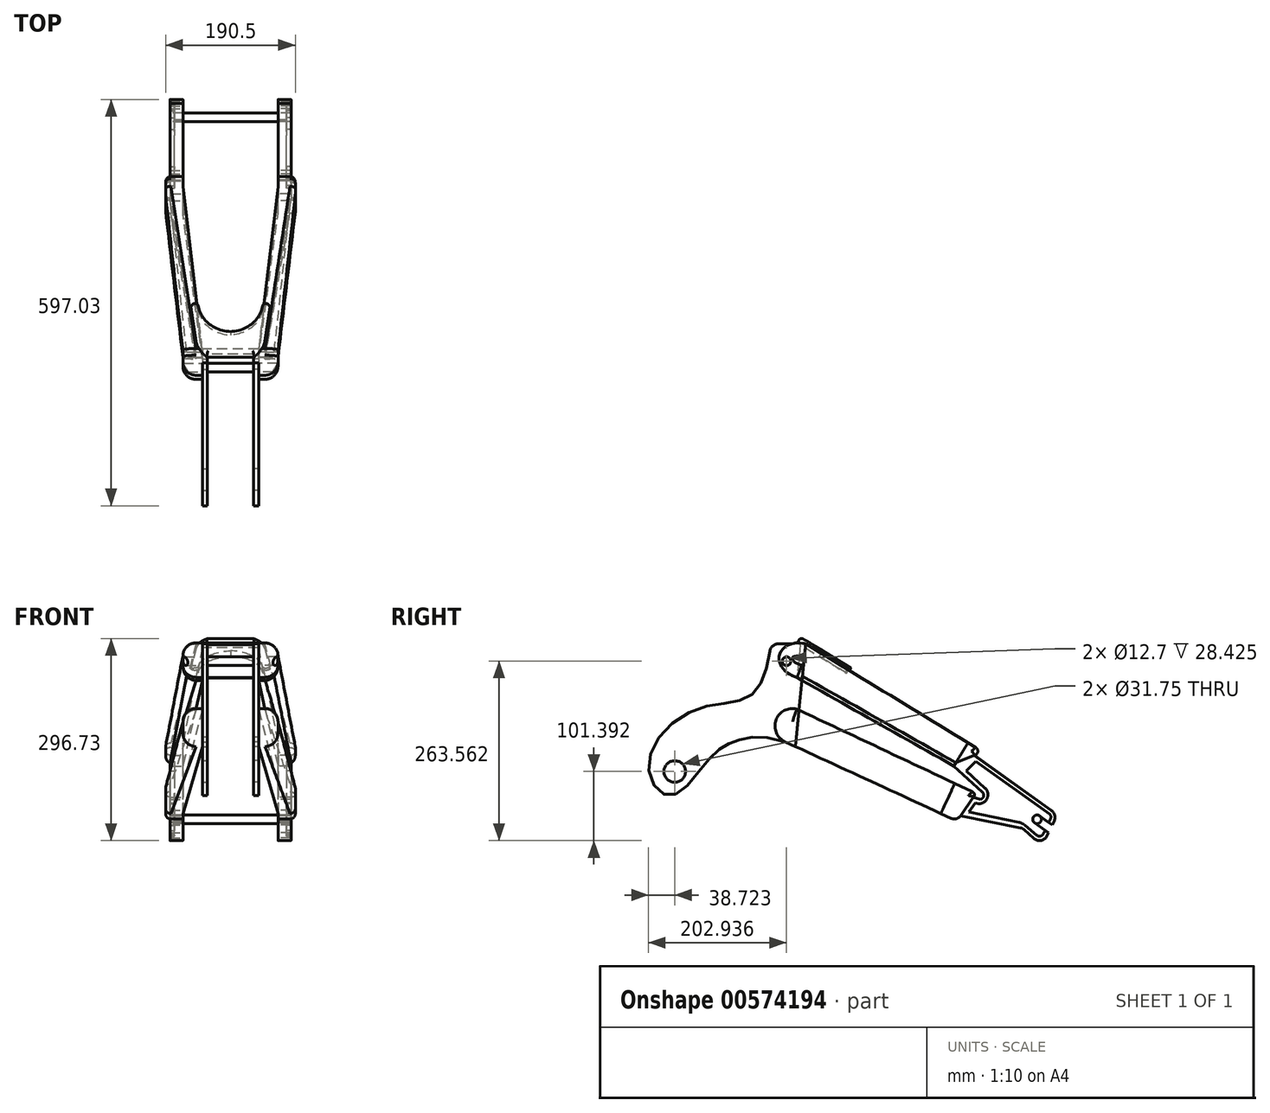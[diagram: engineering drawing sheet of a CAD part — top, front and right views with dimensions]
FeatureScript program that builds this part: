
annotation { "Feature Type Name" : "Feature", "Feature Type Description" : "" }
export const myFeature = defineFeature(function(context is Context, id is Id, definition is map)
    precondition{}
    {
        {
            var Q0;
            Q0=qCreatedBy(makeId("Right.planeOp"),FACE);
            var sketch = newSketch(context, id + "F0", { "sketchPlane" : qUnion([Q0])});
            skCircle(sketch, "E0", {"center": v(0, 0) * mm, "radius": 1.16 * mm, "construction": true});
            skLineSegment(sketch, "E1", {"start": v(-232.88, 679.32) * mm, "end": v(-270.07, 627.86) * mm, "construction": true});
            skLineSegment(sketch, "E2", {"start": v(-270.07, 627.86) * mm, "end": v(-307.27, 576.4) * mm, "construction": true});
            skLineSegment(sketch, "E3", {"start": v(-307.27, 576.4) * mm, "end": v(-723.9, 0) * mm, "construction": true});
            skLineSegment(sketch, "E4", {"start": v(-270.07, 627.86) * mm, "end": v(185.67, 350.7) * mm, "construction": true});
            skCircle(sketch, "E5", {"center": v(0, 0) * mm, "radius": 12.7 * mm});
            skCircle(sketch, "E6", {"center": v(-78.13, 64.95) * mm, "radius": 15.88 * mm});
            skLineSegment(sketch, "E7", {"start": v(-78.13, 64.95) * mm, "end": v(-64.36, 72.86) * mm, "construction": true});
            skLineSegment(sketch, "E8", {"start": v(107.04, 228.4) * mm, "end": v(360.88, 72.62) * mm, "construction": true});
            skLineSegment(sketch, "E9", {"start": v(360.88, 72.62) * mm, "end": v(465.2, 0) * mm, "construction": true});
            skPoint(sketch, "E10.middle", {"position": v(86.09, 227.12) * mm});
            skLineSegment(sketch, "E11", {"start": v(361.77, 88.47) * mm, "end": v(322.87, 73.33) * mm});
            skLineSegment(sketch, "E12", {"start": v(361.77, 88.47) * mm, "end": v(474.18, 8.33) * mm});
            skLineSegment(sketch, "E13.trimOffspring", {"start": v(435.13, -20.68) * mm, "end": v(448.92, -33.16) * mm});
            skPoint(sketch, "E14.visualSharp", {"position": v(485.86, 0) * mm});
            skPoint(sketch, "E15.visualSharp", {"position": v(461.59, -44.63) * mm});
            skArc(sketch, "E15.filletArc", {"start": v(448.92, -33.16) * mm, "mid": v(458.05, -36.43) * mm, "end": v(466.83, -32.3) * mm});
            skPoint(sketch, "E16.visualSharp", {"position": v(430.6, -16.57) * mm});
            skArc(sketch, "E16.filletArc", {"start": v(435.13, -20.68) * mm, "mid": v(432.34, -18.76) * mm, "end": v(429.13, -17.64) * mm});
            skPoint(sketch, "E17.visualSharp", {"position": v(384.46, 25.2) * mm});
            skCircle(sketch, "E18", {"center": v(0, 0) * mm, "radius": 22.23 * mm});
            skEllipticalArc(sketch, "E19", {});
            skLineSegment(sketch, "E20", {"start": v(132.64, 242.15) * mm, "end": v(363.9, 100.23) * mm});
            skLineSegment(sketch, "E21", {"start": v(101.4, 203.35) * mm, "end": v(311.62, 74.34) * mm});
            skLineSegment(sketch, "E22", {"start": v(362.88, 88.9) * mm, "end": v(322.87, 73.33) * mm});
            skPoint(sketch, "E23.visualSharp", {"position": v(317, 71.04) * mm});
            skArc(sketch, "E23.filletArc", {"start": v(311.62, 74.34) * mm, "mid": v(317.13, 72.52) * mm, "end": v(322.87, 73.33) * mm});
            skPoint(sketch, "E24.visualSharp", {"position": v(374.8, 93.54) * mm});
            skArc(sketch, "E24.filletArc", {"start": v(362.88, 88.9) * mm, "mid": v(366.9, 94.25) * mm, "end": v(363.9, 100.23) * mm});
            skLineSegment(sketch, "E25", {"start": v(326.7, 65.1) * mm, "end": v(352.54, 107.2) * mm});
            skArc(sketch, "E26.1", {"start": v(473.17, -5.57) * mm, "mid": v(474.21, -1.37) * mm, "end": v(472.33, 2.52) * mm});
            skLineSegment(sketch, "E26.2", {"start": v(364.06, 79.7) * mm, "end": v(472.33, 2.52) * mm});
            skLineSegment(sketch, "E26.3", {"start": v(364.06, 79.7) * mm, "end": v(349.79, 65.87) * mm});
            skArc(sketch, "E26.4", {"start": v(436.25, -14.18) * mm, "mid": v(432.06, -11.3) * mm, "end": v(427.25, -9.63) * mm});
            skLineSegment(sketch, "E26.8", {"start": v(353.82, 5.27) * mm, "end": v(427.25, -9.63) * mm});
            skLineSegment(sketch, "E26.9", {"start": v(353.82, 5.27) * mm, "end": v(353.82, 5.27) * mm});
            skLineSegment(sketch, "E26.10", {"start": v(353.82, 5.27) * mm, "end": v(363.3, 18.82) * mm});
            skLineSegment(sketch, "E26.13", {"start": v(349.79, 65.87) * mm, "end": v(377.5, 40.5) * mm});
            skArc(sketch, "E27", {"start": v(106.8, 154) * mm, "mid": v(105.6, 154.53) * mm, "end": v(104.38, 155) * mm});
            skPoint(sketch, "E28.visualSharp", {"position": v(367.54, 96.52) * mm});
            skPoint(sketch, "E29.visualSharp", {"position": v(357.72, 48.2) * mm});
            skPoint(sketch, "E30.0.internal.orphan", {"position": v(62.7, 11.08) * mm});
            skPoint(sketch, "E30.endDerivative.orphan", {"position": v(0, 109.86) * mm});
            skCircle(sketch, "E31", {"center": v(86.09, 227.12) * mm, "radius": 6.35 * mm});
            skArc(sketch, "E32", {"start": v(223.85, 186.17) * mm, "mid": v(173.06, 140.92) * mm, "end": v(132.63, 86.22) * mm, "construction": true});
            skLineSegment(sketch, "E33", {"start": v(93.24, 252.52) * mm, "end": v(74.1, 252.52) * mm});
            skFitSpline(sketch, "E34", {"points": [v(63.36, 252.52) * mm, v(34.16, 177.27) * mm, v(-50.36, 154.97) * mm, v(-116.85, 72.97) * mm, v(-84.09, 29.6) * mm, v(-25.78, 85.5) * mm, v(12.3, 109.86) * mm, v(83.95, 108.65) * mm], "startDerivative": vector(-99.71, -604.57) * mm, "endDerivative": vector(670.82, -241.51) * mm});
            skArc(sketch, "E35.filletArc", {"start": v(74.1, 252.52) * mm, "mid": v(65.93, 249.54) * mm, "end": v(61.59, 242) * mm});
            skPoint(sketch, "E36.orphan", {"position": v(114.16, 252.52) * mm});
            skPoint(sketch, "E37.trimOffspring.end.orphan", {"position": v(-64.8, 72.62) * mm});
            skPoint(sketch, "E38.endSnap0", {"position": v(466.83, -32.3) * mm});
            skArc(sketch, "E39.trimOffspring", {"start": v(478.77, -8.28) * mm, "mid": v(479.72, 0.92) * mm, "end": v(474.18, 8.33) * mm});
            skLineSegment(sketch, "E40", {"start": v(361.01, 27.86) * mm, "end": v(341.53, 0) * mm});
            skLineSegment(sketch, "E41", {"start": v(359.02, 35.33) * mm, "end": v(106.8, 154) * mm});
            skLineSegment(sketch, "E42", {"start": v(327.78, -3.72) * mm, "end": v(83.95, 108.65) * mm});
            skPoint(sketch, "E43.orphan", {"position": v(116.25, 146.34) * mm});
            skLineSegment(sketch, "E44", {"start": v(114.16, 252.52) * mm, "end": v(99.03, 101.7) * mm});
            skLineSegment(sketch, "E45", {"start": v(470.6, -9.4) * mm, "end": v(457.51, -0.07) * mm});
            skArc(sketch, "E46", {"start": v(457.51, -0.07) * mm, "mid": v(448.65, -1.55) * mm, "end": v(450.14, -10.4) * mm});
            skLineSegment(sketch, "E47", {"start": v(450.14, -10.4) * mm, "end": v(465.87, -21.62) * mm});
            skLineSegment(sketch, "E48", {"start": v(473.17, -5.57) * mm, "end": v(470.6, -9.4) * mm});
            skArc(sketch, "E49.0", {"start": v(453.18, -28.45) * mm, "mid": v(458.69, -29.97) * mm, "end": v(463.19, -26.45) * mm});
            skLineSegment(sketch, "E50", {"start": v(453.18, -28.45) * mm, "end": v(436.25, -14.18) * mm});
            skLineSegment(sketch, "E51", {"start": v(463.19, -26.45) * mm, "end": v(465.87, -21.62) * mm});
            skPoint(sketch, "E52.visualSharp", {"position": v(364.45, 32.77) * mm});
            skArc(sketch, "E52.filletArc", {"start": v(361.01, 27.86) * mm, "mid": v(361.75, 32.06) * mm, "end": v(359.02, 35.33) * mm});
            skPoint(sketch, "E53.visualSharp", {"position": v(336.21, -7.6) * mm});
            skArc(sketch, "E53.filletArc", {"start": v(327.78, -3.72) * mm, "mid": v(335.33, -4.36) * mm, "end": v(341.53, 0) * mm});
            skLineSegment(sketch, "E54", {"start": v(429.13, -17.64) * mm, "end": v(341.61, 0.12) * mm});
            skLineSegment(sketch, "E55", {"start": v(333.06, 47.54) * mm, "end": v(312.65, 3.25) * mm});
            skLineSegment(sketch, "E56", {"start": v(373.48, 34.8) * mm, "end": v(327.72, 76.68) * mm});
            skLineSegment(sketch, "E57", {"start": v(478.77, -8.28) * mm, "end": v(476.22, -13.4) * mm});
            skLineSegment(sketch, "E58", {"start": v(465.87, -21.62) * mm, "end": v(470.5, -24.92) * mm});
            skLineSegment(sketch, "E59", {"start": v(470.6, -9.4) * mm, "end": v(476.22, -13.4) * mm});
            skLineSegment(sketch, "E60.trimOffspring", {"start": v(470.5, -24.92) * mm, "end": v(466.83, -32.3) * mm});
            skLineSegment(sketch, "E61", {"start": v(106.8, 154) * mm, "end": v(101.05, 156.7) * mm});
            skArc(sketch, "E62", {"start": v(101.05, 156.7) * mm, "mid": v(70.54, 140.5) * mm, "end": v(83.95, 108.65) * mm});
            skLineSegment(sketch, "E63", {"start": v(370.63, 24.07) * mm, "end": v(360.23, 26.98) * mm});
            skLineSegment(sketch, "E64", {"start": v(101.4, 203.35) * mm, "end": v(106.46, 253.8) * mm});
            skLineSegment(sketch, "E65", {"start": v(132.64, 242.15) * mm, "end": v(114.16, 252.52) * mm});
            skArc(sketch, "E66", {"start": v(370.63, 24.07) * mm, "mid": v(375.3, 28.58) * mm, "end": v(373.48, 34.8) * mm});
            skLineSegment(sketch, "E67", {"start": v(363.3, 18.82) * mm, "end": v(367.7, 17.76) * mm});
            skArc(sketch, "E68", {"start": v(367.7, 17.76) * mm, "mid": v(380.7, 25.64) * mm, "end": v(377.5, 40.5) * mm});
            const initialGuessF0  = {"E19": [0.10777975644892944, 0.22793694152375826, 0.25127126595347304, 0.967916706595221, 0.0254, 0.03324043917130964, 6.283185307179586, 3.141592653589793]};
            skSetInitialGuess(sketch, initialGuessF0);
            skSolve(sketch);
        }
        {
            var Q0;
            Q0=makeQuery(id+"F0.imprint","IMPRINT",FACE,{"disambiguationData":[TD([[makeQuery(id+"F0.imprint","IMPRINT",EDGE,{"derivedFrom":sQuery(id+"F0.wireOp",EDGE,"E6")}),-1.0]])]});
            var Q1;
            {var subQ3=sQuery(id+"F0.wireOp",EDGE,"E64");Q1=makeQuery(id+"F0.imprint","IMPRINT",FACE,{"disambiguationData":[TD([[makeQuery(id+"F0.imprint","IMPRINT",EDGE,{"derivedFrom":subQ3}),-1.0]])]});}
            var Q2;
            {var subQ2=sQuery(id+"F0.wireOp",EDGE,"E64");Q2=makeQuery(id+"F0.imprint","IMPRINT",FACE,{"disambiguationData":[TD([[makeQuery(id+"F0.imprint","IMPRINT",EDGE,{"derivedFrom":subQ2}),1.0]])]});}
            var Q3;
            {var subQ0=sQuery(id+"F0.wireOp",EDGE,"E62");Q3=makeQuery(id+"F0.imprint","IMPRINT",FACE,{"disambiguationData":[TD([[makeQuery(id+"F0.imprint","IMPRINT",EDGE,{"derivedFrom":subQ0}),1.0]])]});}
            extrude(context, id + "F1", {"entities" : qUnion([Q0, Q1, Q2, Q3]), "oppositeDirection" : true, "depth" : 41.27 * mm, "offsetDistance" : 25.4 * mm, "hasSecondDirection" : true, "secondDirectionOppositeDirection" : true, "secondDirectionDepth" : 34 * mm});
        }
        {
            var Q0;
            {var subQ2=sQuery(id+"F0.wireOp",EDGE,"E64");Q0=makeQuery(id+"F0.imprint","IMPRINT",FACE,{"disambiguationData":[TD([[makeQuery(id+"F0.imprint","IMPRINT",EDGE,{"derivedFrom":subQ2}),1.0]])]});}
            var Q1;
            {var subQ3=sQuery(id+"F0.wireOp",EDGE,"E64");Q1=makeQuery(id+"F0.imprint","IMPRINT",FACE,{"disambiguationData":[TD([[makeQuery(id+"F0.imprint","IMPRINT",EDGE,{"derivedFrom":subQ3}),-1.0]])]});}
            var Q2;
            Q2=makeQuery(id+"F1.opExtrude","CAP_FACE",FACE,{"disambiguationData":[OSD([sQuery(id+"F0.wireOp",EDGE,"E6"),sQuery(id+"F0.wireOp",EDGE,"E19"),sQuery(id+"F0.wireOp",EDGE,"E31"),sQuery(id+"F0.wireOp",EDGE,"E33"),sQuery(id+"F0.wireOp",EDGE,"E34"),sQuery(id+"F0.wireOp",EDGE,"E35.filletArc"),sQuery(id+"F0.wireOp",EDGE,"E42"),sQuery(id+"F0.wireOp",EDGE,"E44")])],"isStart":false});
            var Q3;
            Q3=makeQuery(id+"F1.opExtrude","CAP_FACE",FACE,{"disambiguationData":[OSD([sQuery(id+"F0.wireOp",EDGE,"E6"),sQuery(id+"F0.wireOp",EDGE,"E19"),sQuery(id+"F0.wireOp",EDGE,"E31"),sQuery(id+"F0.wireOp",EDGE,"E33"),sQuery(id+"F0.wireOp",EDGE,"E34"),sQuery(id+"F0.wireOp",EDGE,"E35.filletArc"),sQuery(id+"F0.wireOp",EDGE,"E42"),sQuery(id+"F0.wireOp",EDGE,"E44")])],"isStart":false});
            extrude(context, id + "F2", {"entities" : qUnion([Q0, Q1]), "oppositeDirection" : true, "depth" : 69.85 * mm, "endBoundEntityFace" : qUnion([Q2]), "offsetDistance" : 25.4 * mm, "hasSecondDirection" : true, "secondDirectionOppositeDirection" : true, "secondDirectionDepth" : 41.27 * mm, "secondDirectionBoundEntityFace" : qUnion([Q3])});
        }
        {
            var Q0;
            {var subQ0=sQuery(id+"F0.wireOp",EDGE,"E62");Q0=makeQuery(id+"F0.imprint","IMPRINT",FACE,{"disambiguationData":[TD([[makeQuery(id+"F0.imprint","IMPRINT",EDGE,{"derivedFrom":subQ0}),1.0]])]});}
            var Q1;
            Q1=makeQuery(id+"F1.opExtrude","CAP_FACE",FACE,{"disambiguationData":[OSD([sQuery(id+"F0.wireOp",EDGE,"E6"),sQuery(id+"F0.wireOp",EDGE,"E19"),sQuery(id+"F0.wireOp",EDGE,"E31"),sQuery(id+"F0.wireOp",EDGE,"E33"),sQuery(id+"F0.wireOp",EDGE,"E34"),sQuery(id+"F0.wireOp",EDGE,"E35.filletArc"),sQuery(id+"F0.wireOp",EDGE,"E42"),sQuery(id+"F0.wireOp",EDGE,"E44")])],"isStart":false});
            extrude(context, id + "F3", {"entities" : qUnion([Q0]), "oppositeDirection" : true, "depth" : 69.85 * mm, "offsetDistance" : 25.4 * mm, "hasSecondDirection" : true, "secondDirectionBound" : BoundingType.UP_TO_SURFACE, "secondDirectionOppositeDirection" : true, "secondDirectionDepth" : 41.27 * mm, "secondDirectionBoundEntityFace" : qUnion([Q1])});
        }
        {
            var Q0;
            Q0=makeQuery(id+"F3.opExtrude","CAP_EDGE",EDGE,{"disambiguationData":[OSD([sQuery(id+"F0.wireOp",EDGE,"E42")])],"isStart":false});
            var Q1;
            Q1=makeQuery(id+"F3.opExtrude","CAP_EDGE",EDGE,{"disambiguationData":[OSD([sQuery(id+"F0.wireOp",EDGE,"E62")])],"isStart":false});
            var Q2;
            Q2=makeQuery(id+"F3.opExtrude","CAP_EDGE",EDGE,{"disambiguationData":[OSD([sQuery(id+"F0.wireOp",EDGE,"E61")])],"isStart":false});
            fillet(context, id + "F4", {"entities" : qUnion([Q0, Q1, Q2]), "radius" : 19.05 * mm, "tangentPropagation" : true, "allowEdgeOverflow" : false});
        }
        {
            var Q0;
            Q0=makeQuery(id+"F2.opExtrude","CAP_EDGE",EDGE,{"disambiguationData":[OSD([sQuery(id+"F0.wireOp",EDGE,"E19")])],"isStart":false});
            var Q1;
            Q1=makeQuery(id+"F2.opExtrude","CAP_EDGE",EDGE,{"disambiguationData":[OSD([sQuery(id+"F0.wireOp",EDGE,"E21")])],"isStart":false});
            var Q2;
            Q2=makeQuery(id+"F2.opExtrude","CAP_EDGE",EDGE,{"disambiguationData":[OSD([sQuery(id+"F0.wireOp",EDGE,"E62")])],"isStart":false});
            var Q3;
            Q3=makeQuery(id+"F2.opExtrude","CAP_EDGE",EDGE,{"disambiguationData":[OSD([sQuery(id+"F0.wireOp",EDGE,"E42")])],"isStart":false});
            var Q4;
            Q4=makeQuery(id+"F2.opExtrude","CAP_EDGE",EDGE,{"disambiguationData":[OSD([sQuery(id+"F0.wireOp",EDGE,"E61")])],"isStart":false});
            fillet(context, id + "F5", {"entities" : qUnion([Q0, Q1, Q2, Q3, Q4]), "radius" : 19.05 * mm, "tangentPropagation" : true, "allowEdgeOverflow" : false});
        }
        {
            var Q0;
            {var subQ2=sQuery(id+"F0.wireOp",EDGE,"E12");Q0=makeQuery(id+"F0.imprint","IMPRINT",FACE,{"disambiguationData":[TD([[makeQuery(id+"F0.imprint","IMPRINT",EDGE,{"derivedFrom":subQ2}),-1.0]])]});}
            extrude(context, id + "F6", {"entities" : qUnion([Q0]), "oppositeDirection" : true, "depth" : 82.55 * mm, "offsetDistance" : 25.4 * mm, "hasSecondDirection" : true, "secondDirectionOppositeDirection" : true, "secondDirectionDepth" : 69.85 * mm});
        }
        {
            var Q0;
            {var subQ8=sQuery(id+"F0.wireOp",EDGE,"E12");Q0=makeQuery(id+"F0.imprint","IMPRINT",FACE,{"disambiguationData":[TD([[makeQuery(id+"F0.imprint","IMPRINT",EDGE,{"derivedFrom":subQ8}),-1.0]])]});}
            var Q1;
            Q1=makeQuery(id+"F6.opExtrude","CAP_FACE",FACE,{"disambiguationData":[OSD([sQuery(id+"F0.wireOp",EDGE,"E12"),sQuery(id+"F0.wireOp",EDGE,"M1xsbYhA-3GXW-TK3J-AiRY-MQwu2QjJ6JFv"),sQuery(id+"F0.wireOp",EDGE,"fftMuAfU-lyxI-JiHh-AROv-P9D5QgGa0bzV"),sQuery(id+"F0.wireOp",EDGE,"pFgT3zMJ-KOq2-b6Dw-mOYE-cKnottaSpSPs"),sQuery(id+"F0.wireOp",EDGE,"Kr73LZLk-hWS2-4xuN-lAFo-ImR0NY1b2jm2"),sQuery(id+"F0.wireOp",EDGE,"o7p56DB6-jSA5-HMdE-oMg3-rrhRXBAi4A6l"),sQuery(id+"F0.wireOp",EDGE,"3QQUFEwI-nFqo-oOJl-WeC0-8RtVsm6bbfu0"),sQuery(id+"F0.wireOp",EDGE,"E13.trimOffspring"),sQuery(id+"F0.wireOp",EDGE,"E14.filletArc"),sQuery(id+"F0.wireOp",EDGE,"E15.filletArc"),sQuery(id+"F0.wireOp",EDGE,"E16.filletArc"),sQuery(id+"F0.wireOp",EDGE,"E17.filletArc"),sQuery(id+"F0.wireOp",EDGE,"97rRG8dY-9QWF-S3jQ-TL0d-bcv7SxNfUhuE"),sQuery(id+"F0.wireOp",EDGE,"4e05d5bf-7781-4494-8613-2b51d00994fc"),sQuery(id+"F0.wireOp",EDGE,"fBmHlY9h-KOnv-hHaG-drBH-S4dukekwon05"),sQuery(id+"F0.wireOp",EDGE,"960b2066-a2d9-46c6-8008-59963f1efdcf.trimOffspring"),sQuery(id+"F0.wireOp",EDGE,"E22")])],"isStart":true});
            extrude(context, id + "F7", {"entities" : qUnion([Q0]), "operationType" : NewBodyOperationType.ADD, "oppositeDirection" : true, "depth" : 88.9 * mm, "offsetDistance" : 25.4 * mm, "hasSecondDirection" : true, "secondDirectionOppositeDirection" : true, "secondDirectionDepth" : 69.85 * mm, "secondDirectionBoundEntityFace" : qUnion([Q1])});
        }
        {
            var Q0;
            Q0=makeQuery(id+"F0.imprint","IMPRINT",FACE,{"disambiguationData":[TD([[makeQuery(id+"F0.imprint","IMPRINT",EDGE,{"derivedFrom":sQuery(id+"F0.wireOp",EDGE,"E26.1")}),1.0]])]});
            var Q1;
            Q1=makeQuery(id+"F6.opExtrude","CAP_FACE",FACE,{"disambiguationData":[OSD([sQuery(id+"F0.wireOp",EDGE,"E12"),sQuery(id+"F0.wireOp",EDGE,"pFgT3zMJ-KOq2-b6Dw-mOYE-cKnottaSpSPs"),sQuery(id+"F0.wireOp",EDGE,"Kr73LZLk-hWS2-4xuN-lAFo-ImR0NY1b2jm2"),sQuery(id+"F0.wireOp",EDGE,"o7p56DB6-jSA5-HMdE-oMg3-rrhRXBAi4A6l"),sQuery(id+"F0.wireOp",EDGE,"3QQUFEwI-nFqo-oOJl-WeC0-8RtVsm6bbfu0"),sQuery(id+"F0.wireOp",EDGE,"E13.trimOffspring"),sQuery(id+"F0.wireOp",EDGE,"E14.filletArc"),sQuery(id+"F0.wireOp",EDGE,"E15.filletArc"),sQuery(id+"F0.wireOp",EDGE,"E16.filletArc"),sQuery(id+"F0.wireOp",EDGE,"E17.filletArc"),sQuery(id+"F0.wireOp",EDGE,"97rRG8dY-9QWF-S3jQ-TL0d-bcv7SxNfUhuE"),sQuery(id+"F0.wireOp",EDGE,"fBmHlY9h-KOnv-hHaG-drBH-S4dukekwon05"),sQuery(id+"F0.wireOp",EDGE,"960b2066-a2d9-46c6-8008-59963f1efdcf.trimOffspring"),sQuery(id+"F0.wireOp",EDGE,"E22"),sQuery(id+"F0.wireOp",EDGE,"E26.0"),sQuery(id+"F0.wireOp",EDGE,"E26.1"),sQuery(id+"F0.wireOp",EDGE,"E26.2"),sQuery(id+"F0.wireOp",EDGE,"E26.3"),sQuery(id+"F0.wireOp",EDGE,"E26.4"),sQuery(id+"F0.wireOp",EDGE,"E26.5"),sQuery(id+"F0.wireOp",EDGE,"E26.6"),sQuery(id+"F0.wireOp",EDGE,"E26.7"),sQuery(id+"F0.wireOp",EDGE,"E26.8"),sQuery(id+"F0.wireOp",EDGE,"E26.9"),sQuery(id+"F0.wireOp",EDGE,"E26.10"),sQuery(id+"F0.wireOp",EDGE,"E26.11"),sQuery(id+"F0.wireOp",EDGE,"E26.12"),sQuery(id+"F0.wireOp",EDGE,"E26.13"),sQuery(id+"F0.wireOp",EDGE,"oD7H4SGl-vte9-Riyu-Gu8U-rxnYaFvigUeV")])],"isStart":true});
            extrude(context, id + "F8", {"entities" : qUnion([Q0]), "operationType" : NewBodyOperationType.ADD, "oppositeDirection" : true, "depth" : 82.55 * mm, "offsetDistance" : 25.4 * mm, "hasSecondDirection" : true, "secondDirectionBound" : BoundingType.UP_TO_SURFACE, "secondDirectionOppositeDirection" : true, "secondDirectionDepth" : 25.4 * mm, "secondDirectionBoundEntityFace" : qUnion([Q1])});
        }
        {
            var Q0;
            {var subQ5=sQuery(id+"F0.wireOp",EDGE,"E24.filletArc");Q0=makeQuery(id+"F0.imprint","IMPRINT",FACE,{"disambiguationData":[TD([[makeQuery(id+"F0.imprint","IMPRINT",EDGE,{"derivedFrom":subQ5}),1.0]])]});}
            var Q1;
            {var subQ0=sQuery(id+"F0.wireOp",EDGE,"oD7H4SGl-vte9-Riyu-Gu8U-rxnYaFvigUeV");var subQ1=sQuery(id+"F0.wireOp",EDGE,"E26.13");var subQ2=sQuery(id+"F0.wireOp",EDGE,"E26.12");var subQ3=sQuery(id+"F0.wireOp",EDGE,"E26.11");var subQ4=sQuery(id+"F0.wireOp",EDGE,"E26.10");var subQ5=sQuery(id+"F0.wireOp",EDGE,"E26.9");var subQ6=sQuery(id+"F0.wireOp",EDGE,"E26.8");var subQ7=sQuery(id+"F0.wireOp",EDGE,"E26.7");var subQ8=sQuery(id+"F0.wireOp",EDGE,"E26.6");var subQ9=sQuery(id+"F0.wireOp",EDGE,"E26.5");var subQ10=sQuery(id+"F0.wireOp",EDGE,"E26.4");var subQ11=sQuery(id+"F0.wireOp",EDGE,"E26.3");var subQ12=sQuery(id+"F0.wireOp",EDGE,"E26.2");var subQ13=sQuery(id+"F0.wireOp",EDGE,"E26.1");var subQ14=sQuery(id+"F0.wireOp",EDGE,"E26.0");var subQ15=sQuery(id+"F0.wireOp",EDGE,"E22");var subQ16=sQuery(id+"F0.wireOp",EDGE,"960b2066-a2d9-46c6-8008-59963f1efdcf.trimOffspring");var subQ17=sQuery(id+"F0.wireOp",EDGE,"fBmHlY9h-KOnv-hHaG-drBH-S4dukekwon05");var subQ18=sQuery(id+"F0.wireOp",EDGE,"97rRG8dY-9QWF-S3jQ-TL0d-bcv7SxNfUhuE");var subQ19=sQuery(id+"F0.wireOp",EDGE,"E17.filletArc");var subQ20=sQuery(id+"F0.wireOp",EDGE,"E16.filletArc");var subQ21=sQuery(id+"F0.wireOp",EDGE,"E15.filletArc");var subQ22=sQuery(id+"F0.wireOp",EDGE,"E14.filletArc");var subQ23=sQuery(id+"F0.wireOp",EDGE,"E13.trimOffspring");var subQ24=sQuery(id+"F0.wireOp",EDGE,"3QQUFEwI-nFqo-oOJl-WeC0-8RtVsm6bbfu0");var subQ25=sQuery(id+"F0.wireOp",EDGE,"o7p56DB6-jSA5-HMdE-oMg3-rrhRXBAi4A6l");var subQ26=sQuery(id+"F0.wireOp",EDGE,"Kr73LZLk-hWS2-4xuN-lAFo-ImR0NY1b2jm2");var subQ27=sQuery(id+"F0.wireOp",EDGE,"pFgT3zMJ-KOq2-b6Dw-mOYE-cKnottaSpSPs");var subQ28=sQuery(id+"F0.wireOp",EDGE,"E12");Q1=makeQuery(id+"F8.boolean.opBoolean","MERGE",FACE,{"derivedFrom":[makeQuery(id+"F6.opExtrude","CAP_FACE",FACE,{"disambiguationData":[OSD([subQ28,subQ27,subQ26,subQ25,subQ24,subQ23,subQ22,subQ21,subQ20,subQ19,subQ18,subQ17,subQ16,subQ15,subQ14,subQ13,subQ12,subQ11,subQ10,subQ9,subQ8,subQ7,subQ6,subQ5,subQ4,subQ3,subQ2,subQ1,subQ0])],"isStart":true}),makeQuery(id+"F8.opExtrude","CAP_FACE",FACE,{"disambiguationData":[OSD([subQ28,subQ27,subQ26,subQ25,subQ24,subQ23,subQ22,subQ21,subQ20,subQ19,subQ18,subQ17,subQ16,subQ15,subQ14,subQ13,subQ12,subQ11,subQ10,subQ9,subQ8,subQ7,subQ6,subQ5,subQ4,subQ3,subQ2,subQ1,subQ0])],"isStart":true})]});}
            extrude(context, id + "F9", {"entities" : qUnion([Q0]), "operationType" : NewBodyOperationType.ADD, "oppositeDirection" : true, "depth" : 95.25 * mm, "offsetDistance" : 25.4 * mm, "hasSecondDirection" : true, "secondDirectionBound" : BoundingType.UP_TO_SURFACE, "secondDirectionOppositeDirection" : true, "secondDirectionDepth" : 25.4 * mm, "secondDirectionBoundEntityFace" : qUnion([Q1])});
        }
        {
            var Q0;
            Q0=makeQuery(id+"F9.opExtrude","CAP_EDGE",EDGE,{"disambiguationData":[OSD([sQuery(id+"F0.wireOp",EDGE,"E20")])],"isStart":false});
            fillet(context, id + "F10", {"entities" : qUnion([Q0]), "radius" : 7.62 * mm, "tangentPropagation" : true, "allowEdgeOverflow" : false});
        }
        {
            var Q0;
            {var subQ5=sQuery(id+"F0.wireOp",EDGE,"E40");Q0=makeQuery(id+"F0.imprint","IMPRINT",FACE,{"disambiguationData":[TD([[makeQuery(id+"F0.imprint","IMPRINT",EDGE,{"derivedFrom":subQ5}),-1.0]])]});}
            var Q1;
            {var subQ0=sQuery(id+"F0.wireOp",EDGE,"oD7H4SGl-vte9-Riyu-Gu8U-rxnYaFvigUeV");var subQ1=sQuery(id+"F0.wireOp",EDGE,"E26.13");var subQ2=sQuery(id+"F0.wireOp",EDGE,"E26.12");var subQ3=sQuery(id+"F0.wireOp",EDGE,"E26.11");var subQ4=sQuery(id+"F0.wireOp",EDGE,"E26.10");var subQ5=sQuery(id+"F0.wireOp",EDGE,"E26.9");var subQ6=sQuery(id+"F0.wireOp",EDGE,"E26.8");var subQ7=sQuery(id+"F0.wireOp",EDGE,"E26.7");var subQ8=sQuery(id+"F0.wireOp",EDGE,"E26.6");var subQ9=sQuery(id+"F0.wireOp",EDGE,"E26.5");var subQ10=sQuery(id+"F0.wireOp",EDGE,"E26.4");var subQ11=sQuery(id+"F0.wireOp",EDGE,"E26.3");var subQ12=sQuery(id+"F0.wireOp",EDGE,"E26.2");var subQ13=sQuery(id+"F0.wireOp",EDGE,"E26.1");var subQ14=sQuery(id+"F0.wireOp",EDGE,"E26.0");var subQ15=sQuery(id+"F0.wireOp",EDGE,"E22");var subQ16=sQuery(id+"F0.wireOp",EDGE,"960b2066-a2d9-46c6-8008-59963f1efdcf.trimOffspring");var subQ17=sQuery(id+"F0.wireOp",EDGE,"fBmHlY9h-KOnv-hHaG-drBH-S4dukekwon05");var subQ18=sQuery(id+"F0.wireOp",EDGE,"97rRG8dY-9QWF-S3jQ-TL0d-bcv7SxNfUhuE");var subQ19=sQuery(id+"F0.wireOp",EDGE,"E17.filletArc");var subQ20=sQuery(id+"F0.wireOp",EDGE,"E16.filletArc");var subQ21=sQuery(id+"F0.wireOp",EDGE,"E15.filletArc");var subQ22=sQuery(id+"F0.wireOp",EDGE,"E14.filletArc");var subQ23=sQuery(id+"F0.wireOp",EDGE,"E13.trimOffspring");var subQ24=sQuery(id+"F0.wireOp",EDGE,"3QQUFEwI-nFqo-oOJl-WeC0-8RtVsm6bbfu0");var subQ25=sQuery(id+"F0.wireOp",EDGE,"o7p56DB6-jSA5-HMdE-oMg3-rrhRXBAi4A6l");var subQ26=sQuery(id+"F0.wireOp",EDGE,"Kr73LZLk-hWS2-4xuN-lAFo-ImR0NY1b2jm2");var subQ27=sQuery(id+"F0.wireOp",EDGE,"pFgT3zMJ-KOq2-b6Dw-mOYE-cKnottaSpSPs");var subQ28=sQuery(id+"F0.wireOp",EDGE,"E12");Q1=makeQuery(id+"F9.boolean.opBoolean","MERGE",FACE,{"derivedFrom":[makeQuery(id+"F8.boolean.opBoolean","MERGE",FACE,{"derivedFrom":[makeQuery(id+"F6.opExtrude","CAP_FACE",FACE,{"disambiguationData":[OSD([subQ28,subQ27,subQ26,subQ25,subQ24,subQ23,subQ22,subQ21,subQ20,subQ19,subQ18,subQ17,subQ16,subQ15,subQ14,subQ13,subQ12,subQ11,subQ10,subQ9,subQ8,subQ7,subQ6,subQ5,subQ4,subQ3,subQ2,subQ1,subQ0])],"isStart":true}),makeQuery(id+"F8.opExtrude","CAP_FACE",FACE,{"disambiguationData":[OSD([subQ28,subQ27,subQ26,subQ25,subQ24,subQ23,subQ22,subQ21,subQ20,subQ19,subQ18,subQ17,subQ16,subQ15,subQ14,subQ13,subQ12,subQ11,subQ10,subQ9,subQ8,subQ7,subQ6,subQ5,subQ4,subQ3,subQ2,subQ1,subQ0])],"isStart":true})]}),makeQuery(id+"F9.opExtrude","CAP_FACE",FACE,{"disambiguationData":[OSD([subQ28,subQ27,subQ26,subQ25,subQ24,subQ23,subQ22,subQ21,subQ20,subQ19,subQ18,subQ17,subQ16,subQ15,subQ14,subQ13,subQ12,subQ11,subQ10,subQ9,subQ8,subQ7,subQ6,subQ5,subQ4,subQ3,subQ2,subQ1,subQ0])],"isStart":true})]});}
            extrude(context, id + "F11", {"entities" : qUnion([Q0]), "operationType" : NewBodyOperationType.ADD, "oppositeDirection" : true, "depth" : 95.25 * mm, "offsetDistance" : 25.4 * mm, "hasSecondDirection" : true, "secondDirectionBound" : BoundingType.UP_TO_SURFACE, "secondDirectionOppositeDirection" : true, "secondDirectionDepth" : 25.4 * mm, "secondDirectionBoundEntityFace" : qUnion([Q1])});
        }
        {
            var Q0;
            Q0=makeQuery(id+"F11.opExtrude","CAP_EDGE",EDGE,{"disambiguationData":[OSD([sQuery(id+"F0.wireOp",EDGE,"E40")])],"isStart":false});
            fillet(context, id + "F12", {"entities" : qUnion([Q0]), "radius" : 7.62 * mm, "tangentPropagation" : true, "allowEdgeOverflow" : false});
        }
        {
            var Q0;
            Q0=makeQuery(id+"F2.opExtrude","SWEPT_FACE",FACE,{"disambiguationData":[OSD([sQuery(id+"F0.wireOp",EDGE,"E44")])]});
            var Q1;
            Q1=makeQuery(id+"F9.opExtrude","SWEPT_FACE",FACE,{"disambiguationData":[OSD([sQuery(id+"F0.wireOp",EDGE,"E25")])]});
            loft(context, id + "F13", {"sheetProfilesArray" : [{ "sheetProfileEntities" : qUnion([Q0]) }, { "sheetProfileEntities" : qUnion([Q1]) }]});
        }
        {
            var Q0;
            Q0=makeQuery(id+"F3.opExtrude","SWEPT_FACE",FACE,{"disambiguationData":[OSD([sQuery(id+"F0.wireOp",EDGE,"E44")])]});
            var Q1;
            Q1=makeQuery(id+"F11.opExtrude","SWEPT_FACE",FACE,{"disambiguationData":[OSD([sQuery(id+"F0.wireOp",EDGE,"E55")])]});
            loft(context, id + "F14", {"sheetProfilesArray" : [{ "sheetProfileEntities" : qUnion([Q0]) }, { "sheetProfileEntities" : qUnion([Q1]) }]});
        }
        {
            var Q0;
            Q0=sQuery(id+"F0.wireOp",EDGE,"E8");
            cPlane(context, id + "F15", {"entities" : qUnion([Q0]), "cplaneType" : CPlaneType.LINE_ANGLE, "offset" : 0 * mm, "angle" : 0 * degree, "oppositeDirection" : true, "width" : 152.4 * mm, "height" : 152.4 * mm});
        }
        {
            var Q0;
            Q0=qCreatedBy(id+"F15.planeOp",FACE);
            var sketch = newSketch(context, id + "F16", { "sketchPlane" : qUnion([Q0])});
            skLineSegment(sketch, "E69", {"start": v(0, -46.3) * mm, "end": v(-34.4, -46.3) * mm});
            skPoint(sketch, "E70.visualSharp", {"position": v(-51.04, 53.18) * mm});
            skPoint(sketch, "E71.visualSharp", {"position": v(-105.78, -46.3) * mm});
            skPoint(sketch, "E72.endSnap0", {"position": v(19.63, -11.92) * mm});
            skLineSegment(sketch, "E73", {"start": v(0, -8.2) * mm, "end": v(0, -46.3) * mm});
            skArc(sketch, "E74", {"start": v(-47.07, 36.46) * mm, "mid": v(-31.74, 5.48) * mm, "end": v(0, -8.2) * mm});
            skArc(sketch, "E75", {"start": v(-47.07, 36.46) * mm, "mid": v(-53.25, 40.16) * mm, "end": v(-58.11, 34.85) * mm});
            skLineSegment(sketch, "E76", {"start": v(-58.11, 34.85) * mm, "end": v(-50.77, -21.4) * mm});
            skArc(sketch, "E77", {"start": v(-50.77, -21.4) * mm, "mid": v(-45.45, -35.73) * mm, "end": v(-34.4, -46.3) * mm});
            skSolve(sketch);
        }
        {
            var Q0;
            Q0=makeQuery(id+"F16.imprint","IMPRINT",FACE,{"disambiguationData":[TD([[makeQuery(id+"F16.imprint","IMPRINT",EDGE,{"derivedFrom":sQuery(id+"F16.wireOp",EDGE,"E69")}),-1.0]])]});
            extrude(context, id + "F17", {"entities" : qUnion([Q0]), "depth" : 28.57 * mm, "offsetDistance" : 25.4 * mm, "hasSecondDirection" : true, "secondDirectionOppositeDirection" : false, "secondDirectionDepth" : 19.05 * mm});
        }
        {
            var Q0;
            {var subQ3=sQuery(id+"F0.wireOp",EDGE,"E64");Q0=makeQuery(id+"F0.imprint","IMPRINT",FACE,{"disambiguationData":[TD([[makeQuery(id+"F0.imprint","IMPRINT",EDGE,{"derivedFrom":subQ3}),-1.0]])]});}
            extrude(context, id + "F18", {"entities" : qUnion([Q0]), "operationType" : NewBodyOperationType.ADD, "endBound" : BoundingType.UP_TO_NEXT, "oppositeDirection" : true, "depth" : 25.4 * mm, "offsetDistance" : 25.4 * mm});
        }
        {
            var Q0;
            Q0=makeQuery(id+"F17.opExtrude","CAP_EDGE",EDGE,{"disambiguationData":[OSD([sQuery(id+"F16.wireOp",EDGE,"E69")])],"isStart":false});
            var Q1;
            Q1=makeQuery(id+"F17.opExtrude","CAP_EDGE",EDGE,{"disambiguationData":[OSD([sQuery(id+"F16.wireOp",EDGE,"E77")])],"isStart":false});
            var Q2;
            Q2=makeQuery(id+"F18.opExtrude","SWEPT_EDGE",EDGE,{"disambiguationData":[OSD([sQuery(id+"F0.wireOp",EDGE,"E21"),sQuery(id+"F0.wireOp",EDGE,"E44")])]});
            fillet(context, id + "F19", {"entities" : qUnion([Q0, Q1, Q2]), "radius" : 5.08 * mm, "tangentPropagation" : true, "allowEdgeOverflow" : false});
        }
        {
            var Q0;
            Q0=makeQuery(id+"F3.opExtrude","SWEPT_BODY",BODY,{"disambiguationData":[OSD([sQuery(id+"F0.wireOp",EDGE,"E42"),sQuery(id+"F0.wireOp",EDGE,"E44"),sQuery(id+"F0.wireOp",EDGE,"E61"),sQuery(id+"F0.wireOp",EDGE,"E62")])]});
            var Q1;
            Q1=makeQuery(id+"F14.opLoft","SWEPT_BODY",BODY,{"disambiguationData":[OSD([sQuery(id+"F0.wireOp",EDGE,"E44"),sQuery(id+"F0.wireOp",EDGE,"E55")])]});
            var Q2;
            Q2=makeQuery(id+"F17.opExtrude","SWEPT_BODY",BODY,{"disambiguationData":[OSD([sQuery(id+"F16.wireOp",EDGE,"E69"),sQuery(id+"F16.wireOp",EDGE,"E73"),sQuery(id+"F16.wireOp",EDGE,"E74"),sQuery(id+"F16.wireOp",EDGE,"E75"),sQuery(id+"F16.wireOp",EDGE,"E76"),sQuery(id+"F16.wireOp",EDGE,"E77")])]});
            var Q3;
            Q3=makeQuery(id+"F1.opExtrude","SWEPT_BODY",BODY,{"disambiguationData":[OSD([sQuery(id+"F0.wireOp",EDGE,"E6"),sQuery(id+"F0.wireOp",EDGE,"E19"),sQuery(id+"F0.wireOp",EDGE,"E31"),sQuery(id+"F0.wireOp",EDGE,"E33"),sQuery(id+"F0.wireOp",EDGE,"E34"),sQuery(id+"F0.wireOp",EDGE,"E35.filletArc"),sQuery(id+"F0.wireOp",EDGE,"E42"),sQuery(id+"F0.wireOp",EDGE,"E44")])]});
            var Q4;
            Q4=makeQuery(id+"F13.opLoft","SWEPT_BODY",BODY,{"disambiguationData":[OSD([sQuery(id+"F0.wireOp",EDGE,"E25"),sQuery(id+"F0.wireOp",EDGE,"E44")])]});
            var Q5;
            Q5=makeQuery(id+"F6.opExtrude","SWEPT_BODY",BODY,{"disambiguationData":[OSD([sQuery(id+"F0.wireOp",EDGE,"E12"),sQuery(id+"F0.wireOp",EDGE,"E13.trimOffspring"),sQuery(id+"F0.wireOp",EDGE,"E16.filletArc"),sQuery(id+"F0.wireOp",EDGE,"E22"),sQuery(id+"F0.wireOp",EDGE,"E23.filletArc"),sQuery(id+"F0.wireOp",EDGE,"E26.1"),sQuery(id+"F0.wireOp",EDGE,"E26.2"),sQuery(id+"F0.wireOp",EDGE,"E26.3"),sQuery(id+"F0.wireOp",EDGE,"E26.4"),sQuery(id+"F0.wireOp",EDGE,"E26.8"),sQuery(id+"F0.wireOp",EDGE,"E26.10"),sQuery(id+"F0.wireOp",EDGE,"E26.13"),sQuery(id+"F0.wireOp",EDGE,"E39.trimOffspring"),sQuery(id+"F0.wireOp",EDGE,"E15.filletArc"),sQuery(id+"F0.wireOp",EDGE,"E40"),sQuery(id+"F0.wireOp",EDGE,"E48"),sQuery(id+"F0.wireOp",EDGE,"E49.0"),sQuery(id+"F0.wireOp",EDGE,"E50"),sQuery(id+"F0.wireOp",EDGE,"E51"),sQuery(id+"F0.wireOp",EDGE,"E54"),sQuery(id+"F0.wireOp",EDGE,"E56"),sQuery(id+"F0.wireOp",EDGE,"E57"),sQuery(id+"F0.wireOp",EDGE,"E58"),sQuery(id+"F0.wireOp",EDGE,"E59"),sQuery(id+"F0.wireOp",EDGE,"E60.trimOffspring"),sQuery(id+"F0.wireOp",EDGE,"E63"),sQuery(id+"F0.wireOp",EDGE,"E66"),sQuery(id+"F0.wireOp",EDGE,"E67"),sQuery(id+"F0.wireOp",EDGE,"E68")])]});
            var Q6;
            Q6=makeQuery(id+"F2.opExtrude","SWEPT_BODY",BODY,{"disambiguationData":[OSD([sQuery(id+"F0.wireOp",EDGE,"E19"),sQuery(id+"F0.wireOp",EDGE,"E21"),sQuery(id+"F0.wireOp",EDGE,"E44")])]});
            var Q7;
            Q7=qCreatedBy(makeId("Right.planeOp"),FACE);
            mirror(context, id + "F20", {"operationType" : NewBodyOperationType.ADD, "entities" : qUnion([Q0, Q1, Q2, Q3, Q4, Q5, Q6]), "mirrorPlane" : qUnion([Q7])});
        }
        {
            var Q0;
            Q0=makeQuery(id+"F0.imprint","IMPRINT",FACE,{"disambiguationData":[TD([[makeQuery(id+"F0.imprint","IMPRINT",EDGE,{"derivedFrom":sQuery(id+"F0.wireOp",EDGE,"E31")}),1.0]])]});
            extrude(context, id + "F21", {"entities" : qUnion([Q0]), "operationType" : NewBodyOperationType.ADD, "depth" : 82.55 * mm, "offsetDistance" : 25.4 * mm, "symmetric" : true});
        }
        {
            var Q0;
            Q0=makeQuery(id+"F7.opExtrude","CAP_FACE",FACE,{"disambiguationData":[OSD([sQuery(id+"F0.wireOp",EDGE,"E12"),sQuery(id+"F0.wireOp",EDGE,"E13.trimOffspring"),sQuery(id+"F0.wireOp",EDGE,"E16.filletArc"),sQuery(id+"F0.wireOp",EDGE,"E22"),sQuery(id+"F0.wireOp",EDGE,"E25"),sQuery(id+"F0.wireOp",EDGE,"E26.1"),sQuery(id+"F0.wireOp",EDGE,"E26.2"),sQuery(id+"F0.wireOp",EDGE,"E26.3"),sQuery(id+"F0.wireOp",EDGE,"E26.4"),sQuery(id+"F0.wireOp",EDGE,"E26.8"),sQuery(id+"F0.wireOp",EDGE,"E26.10"),sQuery(id+"F0.wireOp",EDGE,"E26.13"),sQuery(id+"F0.wireOp",EDGE,"E39.trimOffspring"),sQuery(id+"F0.wireOp",EDGE,"E15.filletArc"),sQuery(id+"F0.wireOp",EDGE,"E40"),sQuery(id+"F0.wireOp",EDGE,"E48"),sQuery(id+"F0.wireOp",EDGE,"E49.0"),sQuery(id+"F0.wireOp",EDGE,"E50"),sQuery(id+"F0.wireOp",EDGE,"E51"),sQuery(id+"F0.wireOp",EDGE,"E54"),sQuery(id+"F0.wireOp",EDGE,"E56"),sQuery(id+"F0.wireOp",EDGE,"E57"),sQuery(id+"F0.wireOp",EDGE,"E58"),sQuery(id+"F0.wireOp",EDGE,"E59"),sQuery(id+"F0.wireOp",EDGE,"E60.trimOffspring"),sQuery(id+"F0.wireOp",EDGE,"E63"),sQuery(id+"F0.wireOp",EDGE,"E66"),sQuery(id+"F0.wireOp",EDGE,"E67"),sQuery(id+"F0.wireOp",EDGE,"E68")])],"isStart":false});
            cPlane(context, id + "F22", {"entities" : qUnion([Q0]), "cplaneType" : CPlaneType.OFFSET, "offset" : 25.4 * mm, "width" : 152.4 * mm, "height" : 152.4 * mm});
        }
        {
            var Q0;
            Q0=qCreatedBy(id+"F22.planeOp",FACE);
            var sketch = newSketch(context, id + "F23", { "sketchPlane" : qUnion([Q0])});
            skCircle(sketch, "E78", {"center": v(-453.83, -5.25) * mm, "radius": 6.35 * mm});
            skSolve(sketch);
        }
        {
            var Q0;
            Q0=makeQuery(id+"F23.imprint","IMPRINT",FACE,{"disambiguationData":[TD([[makeQuery(id+"F23.imprint","IMPRINT",EDGE,{"derivedFrom":sQuery(id+"F23.wireOp",EDGE,"E78")}),1.0]])]});
            var Q1;
            Q1=makeQuery(id+"F20.opPattern","COPY",FACE,{"derivedFrom":makeQuery(id+"F7.opExtrude","CAP_FACE",FACE,{"disambiguationData":[OSD([sQuery(id+"F0.wireOp",EDGE,"E12"),sQuery(id+"F0.wireOp",EDGE,"E13.trimOffspring"),sQuery(id+"F0.wireOp",EDGE,"E16.filletArc"),sQuery(id+"F0.wireOp",EDGE,"E22"),sQuery(id+"F0.wireOp",EDGE,"E25"),sQuery(id+"F0.wireOp",EDGE,"E26.1"),sQuery(id+"F0.wireOp",EDGE,"E26.2"),sQuery(id+"F0.wireOp",EDGE,"E26.3"),sQuery(id+"F0.wireOp",EDGE,"E26.4"),sQuery(id+"F0.wireOp",EDGE,"E26.8"),sQuery(id+"F0.wireOp",EDGE,"E26.10"),sQuery(id+"F0.wireOp",EDGE,"E26.13"),sQuery(id+"F0.wireOp",EDGE,"E39.trimOffspring"),sQuery(id+"F0.wireOp",EDGE,"E15.filletArc"),sQuery(id+"F0.wireOp",EDGE,"E40"),sQuery(id+"F0.wireOp",EDGE,"E48"),sQuery(id+"F0.wireOp",EDGE,"E49.0"),sQuery(id+"F0.wireOp",EDGE,"E50"),sQuery(id+"F0.wireOp",EDGE,"E51"),sQuery(id+"F0.wireOp",EDGE,"E54"),sQuery(id+"F0.wireOp",EDGE,"E56"),sQuery(id+"F0.wireOp",EDGE,"E57"),sQuery(id+"F0.wireOp",EDGE,"E58"),sQuery(id+"F0.wireOp",EDGE,"E59"),sQuery(id+"F0.wireOp",EDGE,"E60.trimOffspring"),sQuery(id+"F0.wireOp",EDGE,"E63"),sQuery(id+"F0.wireOp",EDGE,"E66"),sQuery(id+"F0.wireOp",EDGE,"E67"),sQuery(id+"F0.wireOp",EDGE,"E68")])],"isStart":false}),"instanceName":"1"});
            var Q2;
            Q2=makeQuery(id+"F7.opExtrude","CAP_FACE",FACE,{"disambiguationData":[OSD([sQuery(id+"F0.wireOp",EDGE,"E12"),sQuery(id+"F0.wireOp",EDGE,"E13.trimOffspring"),sQuery(id+"F0.wireOp",EDGE,"E16.filletArc"),sQuery(id+"F0.wireOp",EDGE,"E22"),sQuery(id+"F0.wireOp",EDGE,"E25"),sQuery(id+"F0.wireOp",EDGE,"E26.1"),sQuery(id+"F0.wireOp",EDGE,"E26.2"),sQuery(id+"F0.wireOp",EDGE,"E26.3"),sQuery(id+"F0.wireOp",EDGE,"E26.4"),sQuery(id+"F0.wireOp",EDGE,"E26.8"),sQuery(id+"F0.wireOp",EDGE,"E26.10"),sQuery(id+"F0.wireOp",EDGE,"E26.13"),sQuery(id+"F0.wireOp",EDGE,"E39.trimOffspring"),sQuery(id+"F0.wireOp",EDGE,"E15.filletArc"),sQuery(id+"F0.wireOp",EDGE,"E40"),sQuery(id+"F0.wireOp",EDGE,"E48"),sQuery(id+"F0.wireOp",EDGE,"E49.0"),sQuery(id+"F0.wireOp",EDGE,"E50"),sQuery(id+"F0.wireOp",EDGE,"E51"),sQuery(id+"F0.wireOp",EDGE,"E54"),sQuery(id+"F0.wireOp",EDGE,"E56"),sQuery(id+"F0.wireOp",EDGE,"E57"),sQuery(id+"F0.wireOp",EDGE,"E58"),sQuery(id+"F0.wireOp",EDGE,"E59"),sQuery(id+"F0.wireOp",EDGE,"E60.trimOffspring"),sQuery(id+"F0.wireOp",EDGE,"E63"),sQuery(id+"F0.wireOp",EDGE,"E66"),sQuery(id+"F0.wireOp",EDGE,"E67"),sQuery(id+"F0.wireOp",EDGE,"E68")])],"isStart":false});
            extrude(context, id + "F24", {"entities" : qUnion([Q0]), "operationType" : NewBodyOperationType.ADD, "endBound" : BoundingType.UP_TO_SURFACE, "oppositeDirection" : true, "depth" : 25.4 * mm, "endBoundEntityFace" : qUnion([Q1]), "offsetDistance" : 25.4 * mm, "hasSecondDirection" : true, "secondDirectionBound" : BoundingType.UP_TO_SURFACE, "secondDirectionOppositeDirection" : true, "secondDirectionDepth" : 25.4 * mm, "secondDirectionBoundEntityFace" : qUnion([Q2])});
        }
    });
